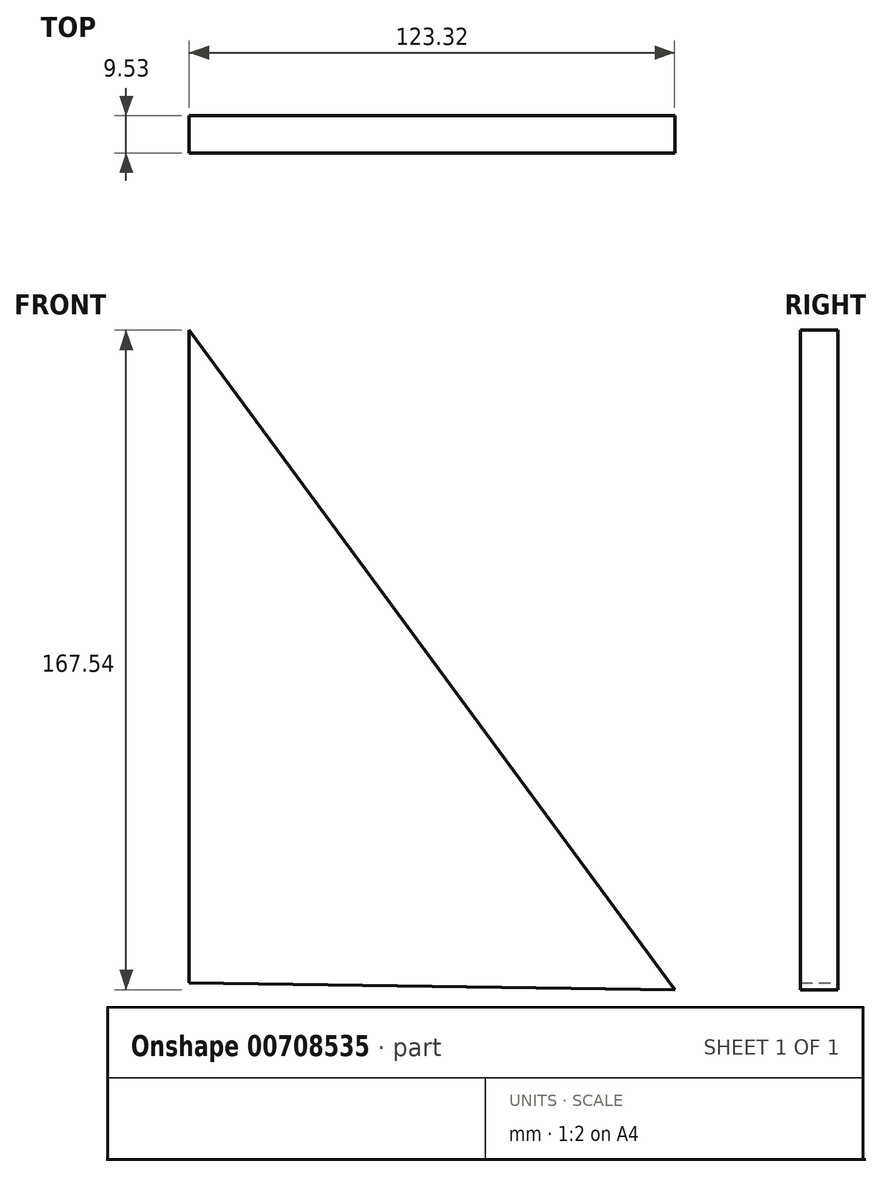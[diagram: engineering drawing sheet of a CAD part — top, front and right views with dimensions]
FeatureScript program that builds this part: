
annotation { "Feature Type Name" : "Feature", "Feature Type Description" : "" }
export const myFeature = defineFeature(function(context is Context, id is Id, definition is map)
    precondition{}
    {
        {
            var Q0;
            Q0=qCreatedBy(makeId("Front.planeOp"),FACE);
            var sketch = newSketch(context, id + "F0", { "sketchPlane" : qUnion([Q0])});
            skLineSegment(sketch, "E0", {"start": v(-68.42, -68.4) * mm, "end": v(-68.42, 97.42) * mm});
            skLineSegment(sketch, "E1", {"start": v(-68.42, 97.42) * mm, "end": v(54.9, -70.12) * mm});
            skLineSegment(sketch, "E2", {"start": v(-68.42, -68.4) * mm, "end": v(54.9, -70.12) * mm});
            skSolve(sketch);
        }
        {
            var Q0;
            Q0=makeQuery(id+"F0.imprint","IMPRINT",FACE,{"disambiguationData":[TD([[makeQuery(id+"F0.imprint","IMPRINT",EDGE,{"derivedFrom":sQuery(id+"F0.wireOp",EDGE,"E0")}),-1.0]])]});
            extrude(context, id + "F1", {"entities" : qUnion([Q0]), "depth" : 9.52 * mm, "offsetDistance" : 25.4 * mm});
        }
    });
